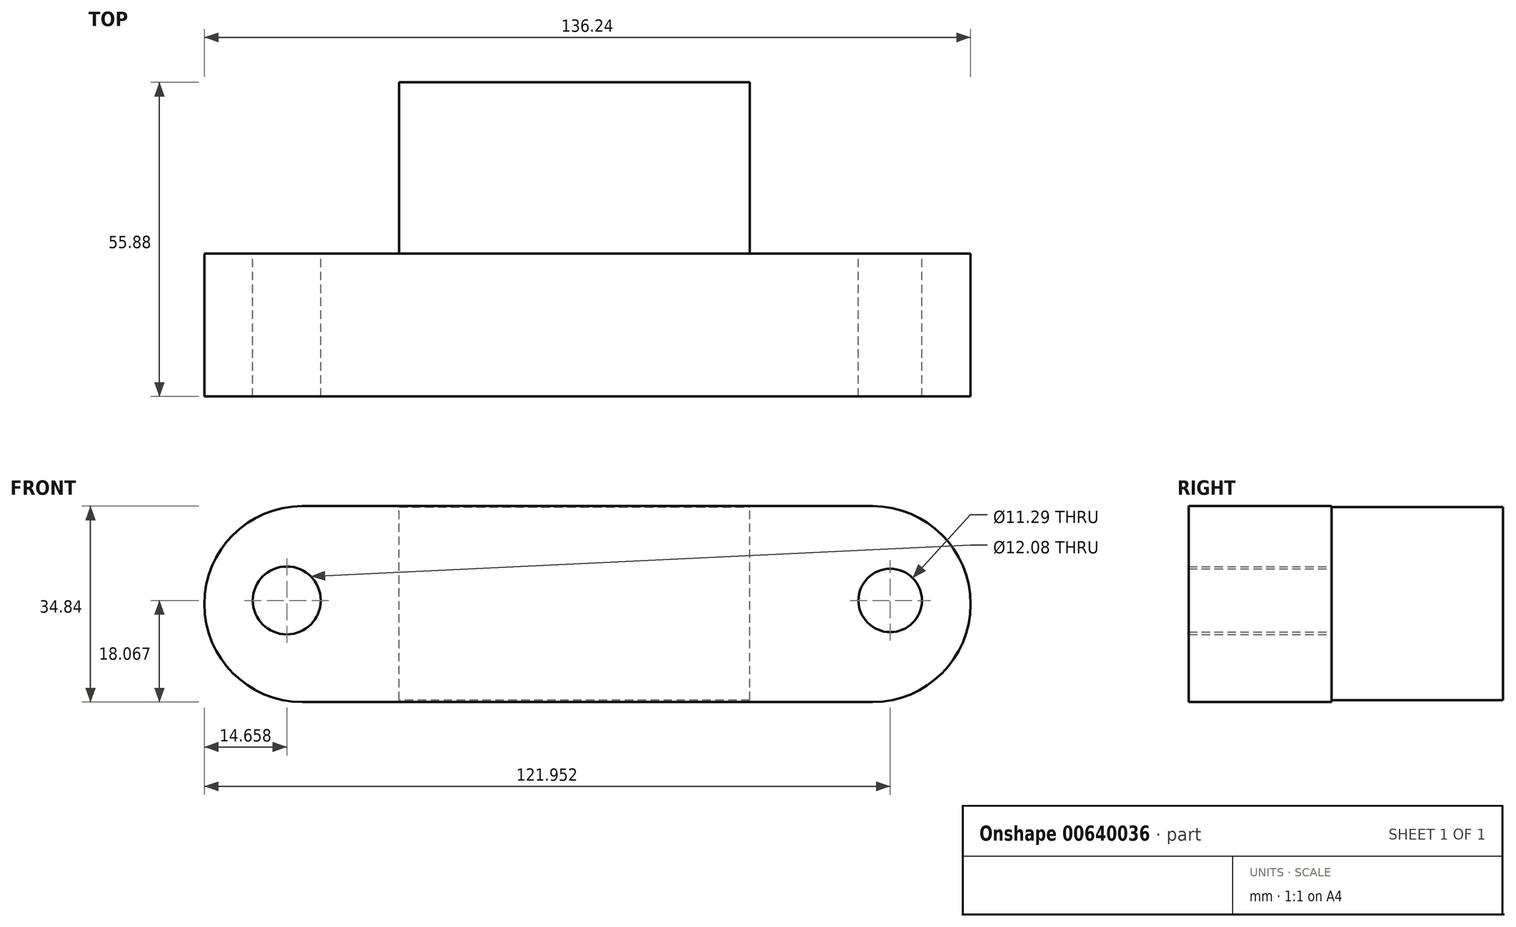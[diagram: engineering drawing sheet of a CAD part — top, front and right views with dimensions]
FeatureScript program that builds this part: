
annotation { "Feature Type Name" : "Feature", "Feature Type Description" : "" }
export const myFeature = defineFeature(function(context is Context, id is Id, definition is map)
    precondition{}
    {
        {
            var Q0;
            Q0=qCreatedBy(makeId("Front.planeOp"),FACE);
            var sketch = newSketch(context, id + "F0", { "sketchPlane" : qUnion([Q0])});
            skLineSegment(sketch, "E0.bottom", {"start": v(-50.24, 11.15) * mm, "end": v(51.16, 11.15) * mm});
            skLineSegment(sketch, "E0.top", {"start": v(-50.24, -23.69) * mm, "end": v(51.16, -23.69) * mm});
            skLineSegment(sketch, "E0.left", {"start": v(-50.24, 11.15) * mm, "end": v(-50.24, -23.69) * mm});
            skLineSegment(sketch, "E0.right", {"start": v(51.16, 11.15) * mm, "end": v(51.16, -23.69) * mm});
            skArc(sketch, "E1", {"start": v(-50.24, 11.15) * mm, "mid": v(-67.66, -6.27) * mm, "end": v(-50.24, -23.69) * mm});
            skArc(sketch, "E2", {"start": v(51.16, -23.69) * mm, "mid": v(68.58, -6.27) * mm, "end": v(51.16, 11.15) * mm});
            skSolve(sketch);
        }
        {
            var Q0;
            Q0=makeQuery(id+"F0.imprint","IMPRINT",FACE,{"disambiguationData":[TD([[makeQuery(id+"F0.imprint","IMPRINT",EDGE,{"derivedFrom":sQuery(id+"F0.wireOp",EDGE,"E0.left")}),-1.0]])]});
            var Q1;
            Q1=makeQuery(id+"F0.imprint","IMPRINT",FACE,{"disambiguationData":[TD([[makeQuery(id+"F0.imprint","IMPRINT",EDGE,{"derivedFrom":sQuery(id+"F0.wireOp",EDGE,"E0.bottom")}),-1.0]])]});
            var Q2;
            Q2=makeQuery(id+"F0.imprint","IMPRINT",FACE,{"disambiguationData":[TD([[makeQuery(id+"F0.imprint","IMPRINT",EDGE,{"derivedFrom":sQuery(id+"F0.wireOp",EDGE,"E0.right")}),1.0]])]});
            extrude(context, id + "F1", {"entities" : qUnion([Q0, Q1, Q2]), "depth" : 25.4 * mm, "offsetDistance" : 25.4 * mm});
        }
        {
            var Q0;
            Q0=qCreatedBy(makeId("Front.planeOp"),FACE);
            var sketch = newSketch(context, id + "F2", { "sketchPlane" : qUnion([Q0])});
            skCircle(sketch, "E3", {"center": v(-53, -5.62) * mm, "radius": 6.04 * mm});
            skCircle(sketch, "E4", {"center": v(54.3, -5.62) * mm, "radius": 5.64 * mm});
            skSolve(sketch);
        }
        {
            var Q0;
            Q0=makeQuery(id+"F2.imprint","IMPRINT",FACE,{"disambiguationData":[TD([[makeQuery(id+"F2.imprint","IMPRINT",EDGE,{"derivedFrom":sQuery(id+"F2.wireOp",EDGE,"E3")}),1.0]])]});
            var Q1;
            Q1=makeQuery(id+"F2.imprint","IMPRINT",FACE,{"disambiguationData":[TD([[makeQuery(id+"F2.imprint","IMPRINT",EDGE,{"derivedFrom":sQuery(id+"F2.wireOp",EDGE,"E4")}),1.0]])]});
            extrude(context, id + "F3", {"entities" : qUnion([Q0, Q1]), "operationType" : NewBodyOperationType.REMOVE, "depth" : 47 * mm, "offsetDistance" : 25.4 * mm});
        }
        {
            var Q0;
            Q0=qCreatedBy(makeId("Front.planeOp"),FACE);
            var sketch = newSketch(context, id + "F4", { "sketchPlane" : qUnion([Q0])});
            skLineSegment(sketch, "E5.top", {"start": v(-33.05, 10.98) * mm, "end": v(29.3, 10.98) * mm});
            skLineSegment(sketch, "E5.left", {"start": v(-33.05, 11.22) * mm, "end": v(-33.05, 10.98) * mm});
            skLineSegment(sketch, "E5.right", {"start": v(29.3, 11.22) * mm, "end": v(29.3, 10.98) * mm});
            skLineSegment(sketch, "E6.bottom", {"start": v(29.3, -23.35) * mm, "end": v(-33.05, -23.35) * mm});
            skLineSegment(sketch, "E6.left", {"start": v(29.3, -23.35) * mm, "end": v(29.3, 10.98) * mm});
            skLineSegment(sketch, "E6.right", {"start": v(-33.05, -23.35) * mm, "end": v(-33.05, 10.98) * mm});
            skSolve(sketch);
        }
        {
            var Q0;
            Q0 = qSketchRegion(id + "F4", true);
            extrude(context, id + "F5", {"entities" : qUnion([Q0]), "operationType" : NewBodyOperationType.ADD, "oppositeDirection" : true, "depth" : 30.48 * mm, "offsetDistance" : 25.4 * mm});
        }
    });
